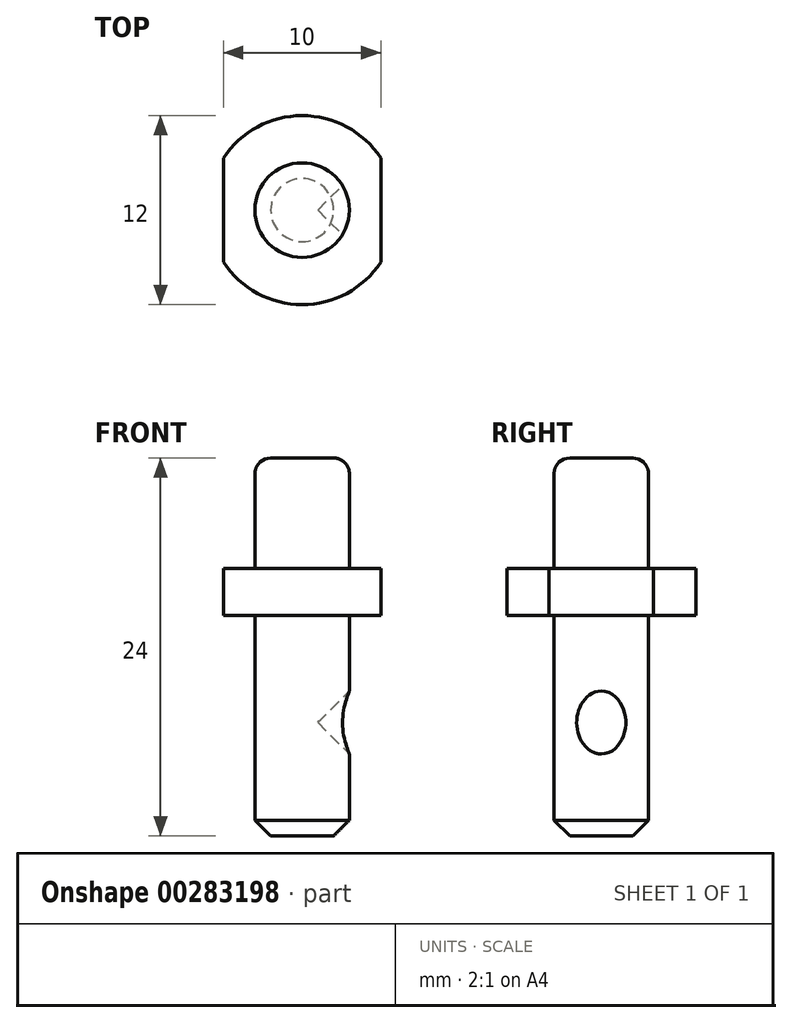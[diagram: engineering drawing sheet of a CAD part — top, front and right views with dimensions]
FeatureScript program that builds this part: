
annotation { "Feature Type Name" : "Feature", "Feature Type Description" : "" }
export const myFeature = defineFeature(function(context is Context, id is Id, definition is map)
    precondition{}
    {
        {
            var Q0;
            Q0=qCreatedBy(makeId("Top.planeOp"),FACE);
            var sketch = newSketch(context, id + "F0", { "sketchPlane" : qUnion([Q0])});
            skCircle(sketch, "E0", {"center": v(0, 0) * mm, "radius": 3 * mm});
            skSolve(sketch);
        }
        {
            var Q0;
            Q0 = qSketchRegion(id + "F0", true);
            extrude(context, id + "F1", {"entities" : qUnion([Q0]), "depth" : 14 * mm});
        }
        {
            var Q0;
            Q0=makeQuery(id+"F1.opExtrude","CAP_FACE",FACE,{"disambiguationData":[OSD([sQuery(id+"F0.wireOp",EDGE,"E0")])],"isStart":false});
            var sketch = newSketch(context, id + "F2", { "sketchPlane" : qUnion([Q0])});
            skArc(sketch, "E1", {"start": v(-5, -3.32) * mm, "mid": v(0, -6) * mm, "end": v(5, -3.32) * mm});
            skLineSegment(sketch, "E2", {"start": v(-5, 3.32) * mm, "end": v(-5, -3.32) * mm});
            skLineSegment(sketch, "E3", {"start": v(5, 3.32) * mm, "end": v(5, -3.32) * mm});
            skArc(sketch, "E4.trimOffspring", {"start": v(5, 3.32) * mm, "mid": v(0, 6) * mm, "end": v(-5, 3.32) * mm});
            skSolve(sketch);
        }
        {
            var Q0;
            Q0 = qSketchRegion(id + "F2", true);
            extrude(context, id + "F3", {"entities" : qUnion([Q0]), "operationType" : NewBodyOperationType.ADD, "depth" : 3 * mm});
        }
        {
            var Q0;
            Q0=makeQuery(id+"F3.opExtrude","CAP_FACE",FACE,{"disambiguationData":[OSD([sQuery(id+"F2.wireOp",EDGE,"E1"),sQuery(id+"F2.wireOp",EDGE,"E2"),sQuery(id+"F2.wireOp",EDGE,"E3"),sQuery(id+"F2.wireOp",EDGE,"E4.trimOffspring")])],"isStart":false});
            var sketch = newSketch(context, id + "F4", { "sketchPlane" : qUnion([Q0])});
            skCircle(sketch, "E5", {"center": v(0, 0) * mm, "radius": 3 * mm});
            skSolve(sketch);
        }
        {
            var Q0;
            Q0 = qSketchRegion(id + "F4", true);
            extrude(context, id + "F5", {"entities" : qUnion([Q0]), "operationType" : NewBodyOperationType.ADD, "depth" : 7 * mm});
        }
        {
            var Q0;
            Q0=makeQuery(id+"F5.opExtrude","CAP_EDGE",EDGE,{"disambiguationData":[OSD([sQuery(id+"F4.wireOp",EDGE,"E5")])],"isStart":false});
            fillet(context, id + "F6", {"entities" : qUnion([Q0]), "radius" : 1 * mm, "tangentPropagation" : true, "allowEdgeOverflow" : false});
        }
        {
            var Q0;
            Q0=qCreatedBy(makeId("Right.planeOp"),FACE);
            cPlane(context, id + "F7", {"entities" : qUnion([Q0]), "cplaneType" : CPlaneType.OFFSET, "offset" : 3 * mm, "width" : 150 * mm, "height" : 150 * mm});
        }
        {
            var Q0;
            Q0=qCreatedBy(id+"F7.planeOp",FACE);
            var sketch = newSketch(context, id + "F8", { "sketchPlane" : qUnion([Q0])});
            skCircle(sketch, "E6", {"center": v(0, 7.2) * mm, "radius": 2 * mm});
            skSolve(sketch);
        }
        {
            var Q0;
            Q0 = qSketchRegion(id + "F8", true);
            extrude(context, id + "F9", {"entities" : qUnion([Q0]), "operationType" : NewBodyOperationType.REMOVE, "oppositeDirection" : true, "depth" : 2 * mm, "hasDraft" : true, "draftAngle" : 45 * degree, "draftPullDirection" : true});
        }
        {
            var Q0;
            Q0=makeQuery(id+"F1.opExtrude","CAP_EDGE",EDGE,{"disambiguationData":[OSD([sQuery(id+"F0.wireOp",EDGE,"E0")])],"isStart":true});
            chamfer(context, id + "F10", {"entities" : qUnion([Q0]), "width" : 1 * mm, "tangentPropagation" : true});
        }
    });
